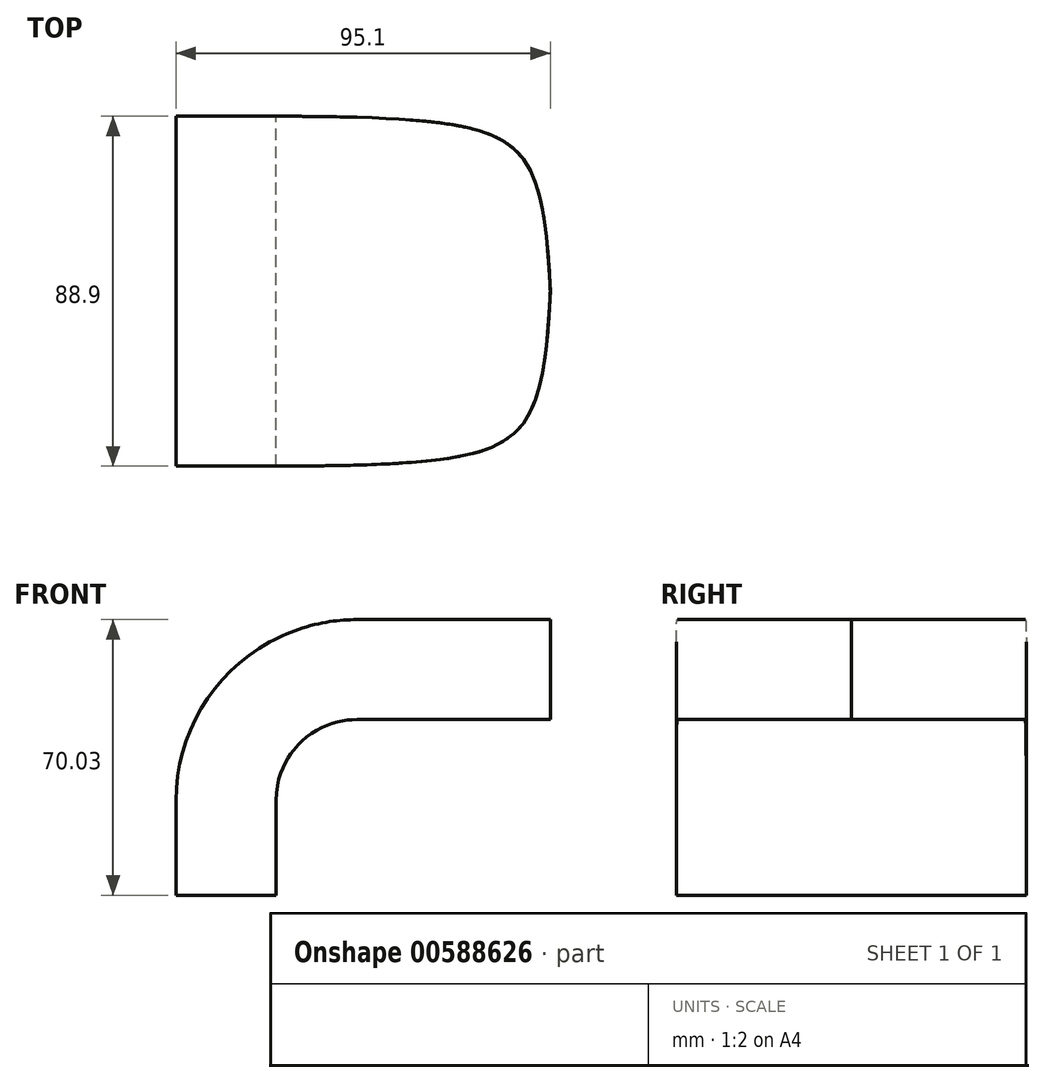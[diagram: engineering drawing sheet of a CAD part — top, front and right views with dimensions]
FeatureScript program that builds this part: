
annotation { "Feature Type Name" : "Feature", "Feature Type Description" : "" }
export const myFeature = defineFeature(function(context is Context, id is Id, definition is map)
    precondition{}
    {
        {
            var Q0;
            Q0=qCreatedBy(makeId("Front.planeOp"),FACE);
            var sketch = newSketch(context, id + "F0", { "sketchPlane" : qUnion([Q0])});
            skLineSegment(sketch, "E0", {"start": v(0, 0) * mm, "end": v(0, 24.08) * mm});
            skArc(sketch, "E1", {"start": v(0, 24.08) * mm, "mid": v(6.02, 38.61) * mm, "end": v(20.55, 44.63) * mm});
            skLineSegment(sketch, "E2", {"start": v(20.55, 44.63) * mm, "end": v(70.15, 44.63) * mm});
            skLineSegment(sketch, "E3.0", {"start": v(20.55, 70.03) * mm, "end": v(70.15, 70.03) * mm});
            skArc(sketch, "E3.1", {"start": v(-25.4, 24.08) * mm, "mid": v(-11.94, 56.57) * mm, "end": v(20.55, 70.03) * mm});
            skLineSegment(sketch, "E3.2", {"start": v(-25.4, 0) * mm, "end": v(-25.4, 24.08) * mm});
            skLineSegment(sketch, "E4", {"start": v(70.15, 44.63) * mm, "end": v(70.15, 70.03) * mm});
            skLineSegment(sketch, "E5", {"start": v(0, 0) * mm, "end": v(-25.4, 0) * mm});
            skSolve(sketch);
        }
        {
            var Q0;
            Q0 = qSketchRegion(id + "F0", true);
            extrude(context, id + "F1", {"entities" : qUnion([Q0]), "depth" : 88.9 * mm, "offsetDistance" : 25.4 * mm});
        }
        {
            var Q0;
            Q0=makeQuery(id+"F1.opExtrude","CAP_EDGE",EDGE,{"disambiguationData":[OSD([sQuery(id+"F0.wireOp",EDGE,"E4")])],"isStart":false});
            var Q1;
            Q1=makeQuery(id+"F1.opExtrude","CAP_EDGE",EDGE,{"disambiguationData":[OSD([sQuery(id+"F0.wireOp",EDGE,"E4")])],"isStart":true});
            fillet(context, id + "F2", {"entities" : qUnion([Q0, Q1]), "radius" : 71.75 * mm, "tangentPropagation" : true, "rho" : .75, "crossSection" : FilletCrossSection.CONIC, "allowEdgeOverflow" : false});
        }
    });
